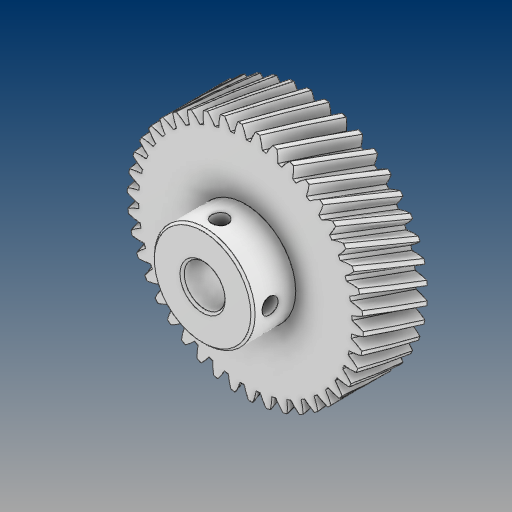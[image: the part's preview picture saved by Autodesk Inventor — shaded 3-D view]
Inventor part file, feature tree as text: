
AUTODESK INVENTOR PART (.ipt)
format: ipt  version: 2021 (Build 250183000, 183)  size: 929,792 bytes
history: native  units: mm (DEFAULTED — no unit token found)
features: extrude x4, sketch x4, plane x3, other x3, chamfer x2, projected_geometry x2, pattern_circular x1
ambient origin geometry x8: Origin, YZ Plane, XZ Plane, XY Plane, X Axis, Y Axis, Z Axis, Center Point
bodies: Solid1 (feature_tree)
feature tree (19):
  extrude  "Extrusion1"  Depth=15.0mm TaperAngle=0.0deg
  plane  "Work Plane2"
  plane  "Work Plane8"
  plane  "Work Plane9"
  other  "Spur Gear"
  sketch  "Sketch3"  dims[d16=45.0mm d17=0.0mm d34=0.747998mm]
  extrude  "Extrusion2"  Depth=10.0mm TaperAngle=0.0deg
  extrude  "Extrusion3"  Depth=0.747998mm TaperAngle=0.0deg
  extrude  "Extrusion4"  TaperAngle=0.0deg  [1 undecoded]
  pattern_circular  "Circular Pattern1"  [2 undecoded]
  chamfer  "Chamfer1"  Distance=45.0mm
  chamfer  "Chamfer2"  [1 undecoded]
  sketch  "Sketch1"  dims[d0=55.253778mm d1=15.0mm d2=0.0mm]
  sketch  "Sketch2"  dims[d3=55.869333mm d4=10.0mm d5=0.0mm]
  other  "Srf1"
  projected_geometry  "Projected Loop1"
  sketch  "Sketch4"  dims[d39=0.0mm d41=0.0mm d43=45.0mm d46=45.0mm d47=0.0mm d48=0.0mm d49=7.0mm d50=9.6mm d51=0.0mm d52=0.0mm d53=10.0mm d54=0.0mm d55=4.0mm d56=3.8mm d57=0.0mm d58=0.0mm d59=20.0mm d60=90.0deg d62=0.5mm d63=2.0mm d64=45.0deg d65=0.5mm d66=2.0mm d67=45.0deg]
  projected_geometry  "Projected Loop2"
  other  "Pitch Diameter"
note: 4 required parameter values undecoded (feature->parameter linkage not recoverable at this tier; creation-order binding heuristic only, values carry confidence <= 0.55)
